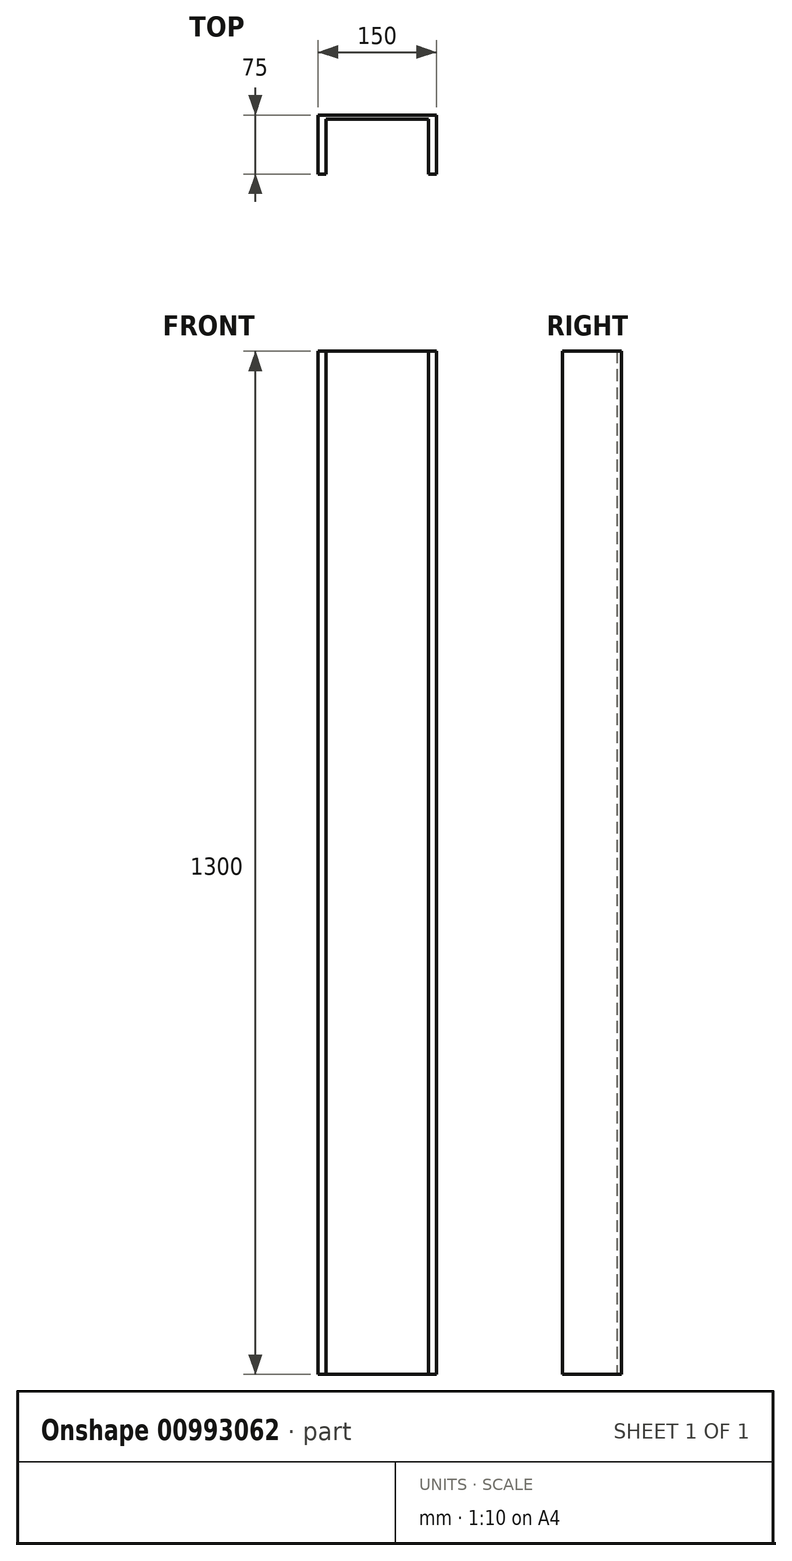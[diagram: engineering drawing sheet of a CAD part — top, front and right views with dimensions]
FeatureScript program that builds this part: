
annotation { "Feature Type Name" : "Feature", "Feature Type Description" : "" }
export const myFeature = defineFeature(function(context is Context, id is Id, definition is map)
    precondition{}
    {
        {
            var Q0;
            Q0=qCreatedBy(makeId("Top.planeOp"),FACE);
            var sketch = newSketch(context, id + "F0", { "sketchPlane" : qUnion([Q0])});
            skLineSegment(sketch, "E0", {"start": v(0, 0) * mm, "end": v(0, 75) * mm});
            skLineSegment(sketch, "E1", {"start": v(0, 75) * mm, "end": v(150, 75) * mm});
            skLineSegment(sketch, "E2", {"start": v(150, 75) * mm, "end": v(150, 0) * mm});
            skLineSegment(sketch, "E3", {"start": v(150, 0) * mm, "end": v(140, 0) * mm});
            skLineSegment(sketch, "E4", {"start": v(140, 0) * mm, "end": v(140, 69.5) * mm});
            skLineSegment(sketch, "E5", {"start": v(140, 69.5) * mm, "end": v(10, 69.5) * mm});
            skLineSegment(sketch, "E6", {"start": v(10, 69.5) * mm, "end": v(10, 0) * mm});
            skLineSegment(sketch, "E7", {"start": v(10, 0) * mm, "end": v(0, 0) * mm});
            skSolve(sketch);
        }
        {
            var Q0;
            Q0=makeQuery(id+"F0.imprint","IMPRINT",FACE,{"disambiguationData":[TD([[makeQuery(id+"F0.imprint","IMPRINT",EDGE,{"derivedFrom":sQuery(id+"F0.wireOp",EDGE,"E0")}),-1.0]])]});
            extrude(context, id + "F1", {"entities" : qUnion([Q0]), "depth" : 1300 * mm, "offsetDistance" : 25 * mm});
        }
    });
